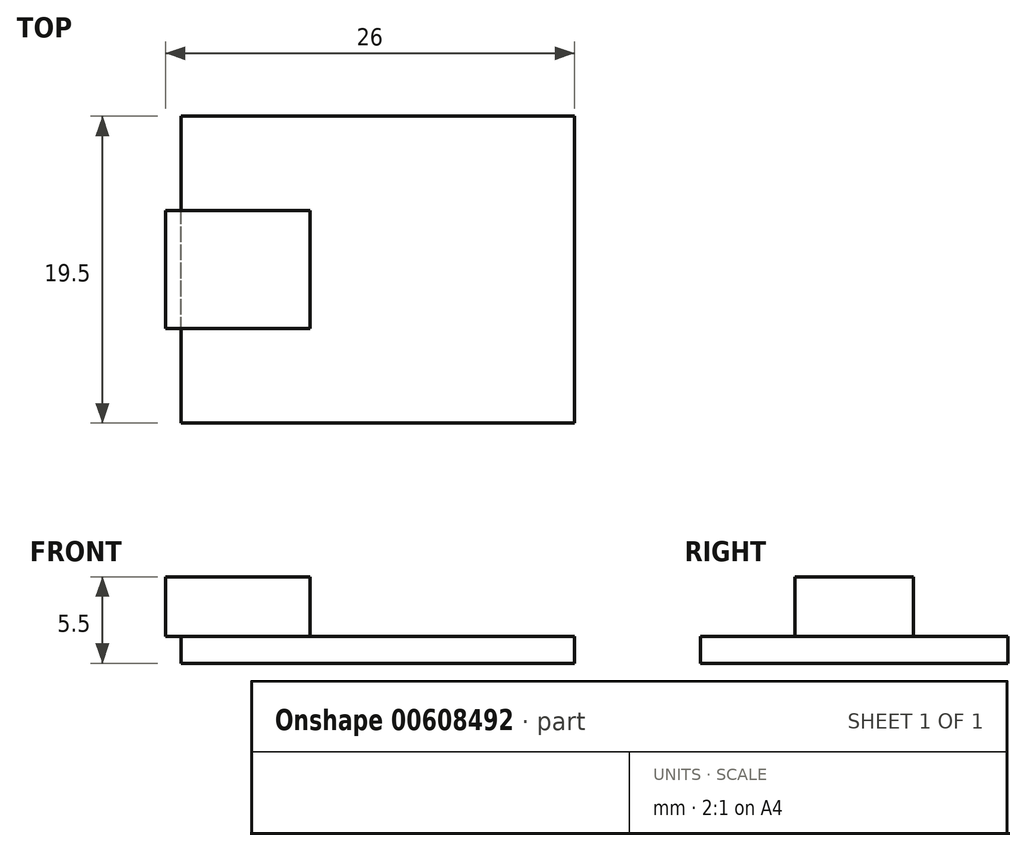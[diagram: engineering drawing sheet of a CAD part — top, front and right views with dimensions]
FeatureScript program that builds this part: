
annotation { "Feature Type Name" : "Feature", "Feature Type Description" : "" }
export const myFeature = defineFeature(function(context is Context, id is Id, definition is map)
    precondition{}
    {
        {
            var Q0;
            Q0=qCreatedBy(makeId("Top.planeOp"),FACE);
            var sketch = newSketch(context, id + "F0", { "sketchPlane" : qUnion([Q0])});
            skLineSegment(sketch, "E0.bottom", {"start": v(12.5, -9.75) * mm, "end": v(-12.5, -9.75) * mm});
            skLineSegment(sketch, "E0.top", {"start": v(12.5, 9.75) * mm, "end": v(-12.5, 9.75) * mm});
            skLineSegment(sketch, "E0.left", {"start": v(12.5, -9.75) * mm, "end": v(12.5, 9.75) * mm});
            skLineSegment(sketch, "E0.right", {"start": v(-12.5, -9.75) * mm, "end": v(-12.5, 9.75) * mm});
            skPoint(sketch, "E0.middle", {"position": v(0, 0) * mm});
            skSolve(sketch);
        }
        {
            var Q0;
            {var subQ1=sQuery(id+"F0.wireOp",EDGE,"E0.bottom");Q0=makeQuery(id+"F0.imprint","IMPRINT",FACE,{"disambiguationData":[TD([[makeQuery(id+"F0.imprint","IMPRINT",EDGE,{"derivedFrom":subQ1}),-1.0]])]});}
            var Q1;
            {var subQ5=sQuery(id+"F0.wireOp",EDGE,"hRiWqytk-cNiW-Dspo-OUKC-hC1kCqK3OtBp.left");Q1=makeQuery(id+"F0.imprint","IMPRINT",FACE,{"disambiguationData":[TD([[makeQuery(id+"F0.imprint","IMPRINT",EDGE,{"derivedFrom":subQ5}),1.0]])]});}
            extrude(context, id + "F1", {"entities" : qUnion([Q0, Q1]), "depth" : 1.7 * mm, "offsetDistance" : 25 * mm});
        }
        {
            var Q0;
            Q0=makeQuery(id+"F1.opExtrude","CAP_FACE",FACE,{"disambiguationData":[OSD([sQuery(id+"F0.wireOp",EDGE,"E0.bottom"),sQuery(id+"F0.wireOp",EDGE,"E0.top"),sQuery(id+"F0.wireOp",EDGE,"E0.left"),sQuery(id+"F0.wireOp",EDGE,"E0.right")])],"isStart":false});
            var sketch = newSketch(context, id + "F2", { "sketchPlane" : qUnion([Q0])});
            skLineSegment(sketch, "E1.bottom", {"start": v(-4.3, -3.75) * mm, "end": v(-13.5, -3.75) * mm});
            skLineSegment(sketch, "E1.top", {"start": v(-4.3, 3.75) * mm, "end": v(-13.5, 3.75) * mm});
            skLineSegment(sketch, "E1.left", {"start": v(-4.3, -3.75) * mm, "end": v(-4.3, 3.75) * mm});
            skLineSegment(sketch, "E1.right", {"start": v(-13.5, -3.75) * mm, "end": v(-13.5, 3.75) * mm});
            skPoint(sketch, "E1.middle", {"position": v(-8.9, 0) * mm});
            skSolve(sketch);
        }
        {
            var Q0;
            Q0 = qSketchRegion(id + "F2", true);
            extrude(context, id + "F3", {"entities" : qUnion([Q0]), "operationType" : NewBodyOperationType.ADD, "depth" : 3.8 * mm, "offsetDistance" : 25 * mm});
        }
    });
